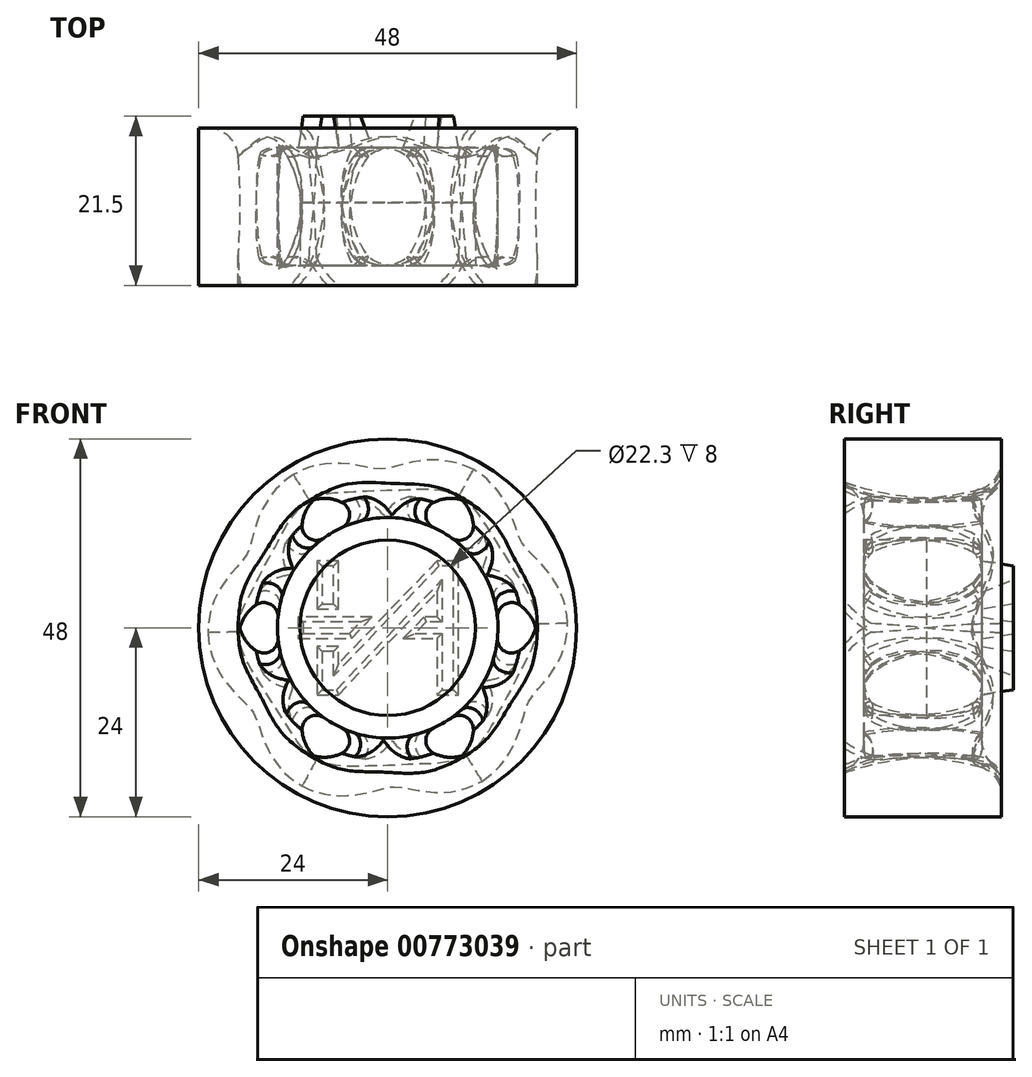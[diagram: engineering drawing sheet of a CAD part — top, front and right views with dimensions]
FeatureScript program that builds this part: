
annotation { "Feature Type Name" : "Feature", "Feature Type Description" : "" }
export const myFeature = defineFeature(function(context is Context, id is Id, definition is map)
    precondition{}
    {
        {
            var Q0;
            Q0=qCreatedBy(makeId("Front.planeOp"),FACE);
            var sketch = newSketch(context, id + "F0", { "sketchPlane" : qUnion([Q0])});
            skCircle(sketch, "E0", {"center": v(0, 0) * mm, "radius": 24 * mm});
            skCircle(sketch, "E1", {"center": v(0, 0) * mm, "radius": 19 * mm});
            skSolve(sketch);
        }
        {
            var Q0;
            Q0 = qSketchRegion(id + "F0", true);
            extrude(context, id + "F1", {"entities" : qUnion([Q0]), "endBound" : BoundingType.SYMMETRIC, "depth" : 20 * mm, "offsetDistance" : 25 * mm});
        }
        {
            var Q0;
            Q0=qCreatedBy(makeId("Front.planeOp"),FACE);
            var sketch = newSketch(context, id + "F2", { "sketchPlane" : qUnion([Q0])});
            skCircle(sketch, "E2", {"center": v(0, 0) * mm, "radius": 14 * mm});
            skSolve(sketch);
        }
        {
            var Q0;
            Q0 = qSketchRegion(id + "F2", true);
            extrude(context, id + "F3", {"entities" : qUnion([Q0]), "endBound" : BoundingType.SYMMETRIC, "depth" : 15 * mm, "offsetDistance" : 25 * mm});
        }
        {
            var Q0;
            Q0=qCreatedBy(makeId("Top.planeOp"),FACE);
            var sketch = newSketch(context, id + "F4", { "sketchPlane" : qUnion([Q0])});
            skEllipse(sketch, "E3", {"center": v(0, 0) * mm, "majorRadius": 7.5 * mm, "minorRadius": 3 * mm, "majorAxis": v(0.08, -1)});
            skSolve(sketch);
        }
        {
            var Q0;
            Q0 = qSketchRegion(id + "F4", true);
            extrude(context, id + "F5", {"entities" : qUnion([Q0]), "depth" : 22.2 * mm, "offsetDistance" : 25 * mm});
        }
        {
            var Q0;
            Q0=makeQuery(id+"F5.opExtrude","SWEPT_BODY",BODY,{"disambiguationData":[OSD([sQuery(id+"F4.wireOp",EDGE,"E3")])]});
            var Q1;
            Q1=makeQuery(id+"F3.opExtrude","CAP_EDGE",EDGE,{"disambiguationData":[OSD([sQuery(id+"F2.wireOp",EDGE,"E2")])],"isStart":true});
            circularPattern(context, id + "F6", {"entities" : qUnion([Q0]), "axis" : qUnion([Q1]), "angle" : 360 * degree, "instanceCount" : 6, "equalSpace" : true});
        }
        {
            var Q0;
            Q0=makeQuery(id+"F3.opExtrude","CAP_FACE",FACE,{"disambiguationData":[OSD([sQuery(id+"F2.wireOp",EDGE,"E2")])],"isStart":false});
            var sketch = newSketch(context, id + "F7", { "sketchPlane" : qUnion([Q0])});
            skPoint(sketch, "E4", {"position": v(0, -1.13) * mm});
            skSolve(sketch);
        }
        {
            var Q0;
            Q0=makeQuery(id+"F7.imprint","IMPRINT",FACE,{"disambiguationData":[TD([[makeQuery(id+"F7.imprint","IMPRINT",EDGE,{"derivedFrom":makeQuery(id+"F3.opExtrude","CAP_EDGE",EDGE,{"disambiguationData":[OSD([sQuery(id+"F2.wireOp",EDGE,"E2")])],"isStart":false})}),1.0]])]});
            var sketch = newSketch(context, id + "F8", { "sketchPlane" : qUnion([Q0])});
            skCircle(sketch, "E5", {"center": v(0, 0) * mm, "radius": 11.15 * mm});
            skSolve(sketch);
        }
        {
            var Q0;
            Q0 = qSketchRegion(id + "F8", true);
            extrude(context, id + "F9", {"entities" : qUnion([Q0]), "operationType" : NewBodyOperationType.REMOVE, "oppositeDirection" : true, "depth" : 8 * mm, "offsetDistance" : 25 * mm});
        }
        {
            var Q0;
            Q0=makeQuery(id+"F3.opExtrude","SWEPT_BODY",BODY,{"disambiguationData":[OSD([sQuery(id+"F2.wireOp",EDGE,"E2")])]});
            var Q1;
            Q1=makeQuery(id+"F1.opExtrude","SWEPT_BODY",BODY,{"disambiguationData":[OSD([sQuery(id+"F0.wireOp",EDGE,"E0"),sQuery(id+"F0.wireOp",EDGE,"E1")])]});
            var Q2;
            Q2=makeQuery(id+"F5.opExtrude","SWEPT_BODY",BODY,{"disambiguationData":[OSD([sQuery(id+"F4.wireOp",EDGE,"E3")])]});
            var Q3;
            Q3=makeQuery(id+"F6.opPattern","COPY",BODY,{"derivedFrom":makeQuery(id+"F5.opExtrude","SWEPT_BODY",BODY,{"disambiguationData":[OSD([sQuery(id+"F4.wireOp",EDGE,"E3")])]}),"instanceName":"2"});
            var Q4;
            Q4=makeQuery(id+"F6.opPattern","COPY",BODY,{"derivedFrom":makeQuery(id+"F5.opExtrude","SWEPT_BODY",BODY,{"disambiguationData":[OSD([sQuery(id+"F4.wireOp",EDGE,"E3")])]}),"instanceName":"4"});
            var Q5;
            Q5=makeQuery(id+"F6.opPattern","COPY",BODY,{"derivedFrom":makeQuery(id+"F5.opExtrude","SWEPT_BODY",BODY,{"disambiguationData":[OSD([sQuery(id+"F4.wireOp",EDGE,"E3")])]}),"instanceName":"5"});
            var Q6;
            Q6=makeQuery(id+"F6.opPattern","COPY",BODY,{"derivedFrom":makeQuery(id+"F5.opExtrude","SWEPT_BODY",BODY,{"disambiguationData":[OSD([sQuery(id+"F4.wireOp",EDGE,"E3")])]}),"instanceName":"1"});
            var Q7;
            Q7=makeQuery(id+"F6.opPattern","COPY",BODY,{"derivedFrom":makeQuery(id+"F5.opExtrude","SWEPT_BODY",BODY,{"disambiguationData":[OSD([sQuery(id+"F4.wireOp",EDGE,"E3")])]}),"instanceName":"3"});
            booleanBodies(context, id + "F10", {"operationType" : BooleanOperationType.UNION, "tools" : qUnion([Q0, Q1, Q2, Q3, Q4, Q5, Q6, Q7])});
        }
        {
            var Q0;
            Q0=makeQuery(id+"F10.opBoolean","INTERSECT",EDGE,{"derivedFrom":[makeQuery(id+"F1.opExtrude","SWEPT_FACE",FACE,{"disambiguationData":[OSD([sQuery(id+"F0.wireOp",EDGE,"E1")])]}),makeQuery(id+"F6.opPattern","COPY",FACE,{"derivedFrom":makeQuery(id+"F5.opExtrude","SWEPT_FACE",FACE,{"disambiguationData":[OSD([sQuery(id+"F4.wireOp",EDGE,"E3")])]}),"instanceName":"2"})]});
            var Q1;
            Q1=makeQuery(id+"F10.opBoolean","INTERSECT",EDGE,{"derivedFrom":[makeQuery(id+"F1.opExtrude","SWEPT_FACE",FACE,{"disambiguationData":[OSD([sQuery(id+"F0.wireOp",EDGE,"E1")])]}),makeQuery(id+"F6.opPattern","COPY",FACE,{"derivedFrom":makeQuery(id+"F5.opExtrude","SWEPT_FACE",FACE,{"disambiguationData":[OSD([sQuery(id+"F4.wireOp",EDGE,"E3")])]}),"instanceName":"3"})]});
            var Q2;
            Q2=makeQuery(id+"F10.opBoolean","INTERSECT",EDGE,{"derivedFrom":[makeQuery(id+"F1.opExtrude","SWEPT_FACE",FACE,{"disambiguationData":[OSD([sQuery(id+"F0.wireOp",EDGE,"E1")])]}),makeQuery(id+"F6.opPattern","COPY",FACE,{"derivedFrom":makeQuery(id+"F5.opExtrude","SWEPT_FACE",FACE,{"disambiguationData":[OSD([sQuery(id+"F4.wireOp",EDGE,"E3")])]}),"instanceName":"4"})]});
            var Q3;
            Q3=makeQuery(id+"F10.opBoolean","INTERSECT",EDGE,{"derivedFrom":[makeQuery(id+"F1.opExtrude","SWEPT_FACE",FACE,{"disambiguationData":[OSD([sQuery(id+"F0.wireOp",EDGE,"E1")])]}),makeQuery(id+"F6.opPattern","COPY",FACE,{"derivedFrom":makeQuery(id+"F5.opExtrude","SWEPT_FACE",FACE,{"disambiguationData":[OSD([sQuery(id+"F4.wireOp",EDGE,"E3")])]}),"instanceName":"5"})]});
            var Q4;
            Q4=makeQuery(id+"F10.opBoolean","INTERSECT",EDGE,{"derivedFrom":[makeQuery(id+"F1.opExtrude","SWEPT_FACE",FACE,{"disambiguationData":[OSD([sQuery(id+"F0.wireOp",EDGE,"E1")])]}),makeQuery(id+"F5.opExtrude","SWEPT_FACE",FACE,{"disambiguationData":[OSD([sQuery(id+"F4.wireOp",EDGE,"E3")])]})]});
            var Q5;
            Q5=makeQuery(id+"F10.opBoolean","INTERSECT",EDGE,{"derivedFrom":[makeQuery(id+"F1.opExtrude","SWEPT_FACE",FACE,{"disambiguationData":[OSD([sQuery(id+"F0.wireOp",EDGE,"E1")])]}),makeQuery(id+"F6.opPattern","COPY",FACE,{"derivedFrom":makeQuery(id+"F5.opExtrude","SWEPT_FACE",FACE,{"disambiguationData":[OSD([sQuery(id+"F4.wireOp",EDGE,"E3")])]}),"instanceName":"1"})]});
            fillet(context, id + "F11", {"entities" : qUnion([Q0, Q1, Q2, Q3, Q4, Q5]), "radius" : 5 * mm, "tangentPropagation" : true, "allowEdgeOverflow" : false});
        }
        {
            var Q0;
            Q0=makeQuery(id+"F11.opFillet","BLEND_EDGE",EDGE,{"disambiguationData":[OD(1.0)],"blendedFrom":[makeQuery(id+"F10.opBoolean","INTERSECT",EDGE,{"derivedFrom":[makeQuery(id+"F1.opExtrude","SWEPT_FACE",FACE,{"disambiguationData":[OSD([sQuery(id+"F0.wireOp",EDGE,"E1")])]}),makeQuery(id+"F6.opPattern","COPY",FACE,{"derivedFrom":makeQuery(id+"F5.opExtrude","SWEPT_FACE",FACE,{"disambiguationData":[OSD([sQuery(id+"F4.wireOp",EDGE,"E3")])]}),"instanceName":"2"})]}),makeQuery(id+"F3.opExtrude","SWEPT_FACE",FACE,{"disambiguationData":[OSD([sQuery(id+"F2.wireOp",EDGE,"E2")])]})],"blendedInto":[makeQuery(id+"F3.opExtrude","SWEPT_FACE",FACE,{"disambiguationData":[OSD([sQuery(id+"F2.wireOp",EDGE,"E2")])]})]});
            var Q1;
            Q1=makeQuery(id+"F11.opFillet","BLEND_EDGE",EDGE,{"disambiguationData":[OD(0.0)],"blendedFrom":[makeQuery(id+"F10.opBoolean","INTERSECT",EDGE,{"derivedFrom":[makeQuery(id+"F1.opExtrude","SWEPT_FACE",FACE,{"disambiguationData":[OSD([sQuery(id+"F0.wireOp",EDGE,"E1")])]}),makeQuery(id+"F6.opPattern","COPY",FACE,{"derivedFrom":makeQuery(id+"F5.opExtrude","SWEPT_FACE",FACE,{"disambiguationData":[OSD([sQuery(id+"F4.wireOp",EDGE,"E3")])]}),"instanceName":"3"})]}),makeQuery(id+"F3.opExtrude","SWEPT_FACE",FACE,{"disambiguationData":[OSD([sQuery(id+"F2.wireOp",EDGE,"E2")])]})],"blendedInto":[makeQuery(id+"F3.opExtrude","SWEPT_FACE",FACE,{"disambiguationData":[OSD([sQuery(id+"F2.wireOp",EDGE,"E2")])]})]});
            var Q2;
            Q2=makeQuery(id+"F11.opFillet","BLEND_EDGE",EDGE,{"disambiguationData":[OD(0.0)],"blendedFrom":[makeQuery(id+"F10.opBoolean","INTERSECT",EDGE,{"derivedFrom":[makeQuery(id+"F1.opExtrude","SWEPT_FACE",FACE,{"disambiguationData":[OSD([sQuery(id+"F0.wireOp",EDGE,"E1")])]}),makeQuery(id+"F6.opPattern","COPY",FACE,{"derivedFrom":makeQuery(id+"F5.opExtrude","SWEPT_FACE",FACE,{"disambiguationData":[OSD([sQuery(id+"F4.wireOp",EDGE,"E3")])]}),"instanceName":"4"})]}),makeQuery(id+"F3.opExtrude","SWEPT_FACE",FACE,{"disambiguationData":[OSD([sQuery(id+"F2.wireOp",EDGE,"E2")])]})],"blendedInto":[makeQuery(id+"F3.opExtrude","SWEPT_FACE",FACE,{"disambiguationData":[OSD([sQuery(id+"F2.wireOp",EDGE,"E2")])]})]});
            var Q3;
            Q3=makeQuery(id+"F11.opFillet","BLEND_EDGE",EDGE,{"disambiguationData":[OD(1.0)],"blendedFrom":[makeQuery(id+"F10.opBoolean","INTERSECT",EDGE,{"derivedFrom":[makeQuery(id+"F1.opExtrude","SWEPT_FACE",FACE,{"disambiguationData":[OSD([sQuery(id+"F0.wireOp",EDGE,"E1")])]}),makeQuery(id+"F6.opPattern","COPY",FACE,{"derivedFrom":makeQuery(id+"F5.opExtrude","SWEPT_FACE",FACE,{"disambiguationData":[OSD([sQuery(id+"F4.wireOp",EDGE,"E3")])]}),"instanceName":"5"})]}),makeQuery(id+"F3.opExtrude","SWEPT_FACE",FACE,{"disambiguationData":[OSD([sQuery(id+"F2.wireOp",EDGE,"E2")])]})],"blendedInto":[makeQuery(id+"F3.opExtrude","SWEPT_FACE",FACE,{"disambiguationData":[OSD([sQuery(id+"F2.wireOp",EDGE,"E2")])]})]});
            var Q4;
            Q4=makeQuery(id+"F11.opFillet","BLEND_EDGE",EDGE,{"disambiguationData":[OD(1.0)],"blendedFrom":[makeQuery(id+"F10.opBoolean","INTERSECT",EDGE,{"derivedFrom":[makeQuery(id+"F1.opExtrude","SWEPT_FACE",FACE,{"disambiguationData":[OSD([sQuery(id+"F0.wireOp",EDGE,"E1")])]}),makeQuery(id+"F5.opExtrude","SWEPT_FACE",FACE,{"disambiguationData":[OSD([sQuery(id+"F4.wireOp",EDGE,"E3")])]})]}),makeQuery(id+"F3.opExtrude","SWEPT_FACE",FACE,{"disambiguationData":[OSD([sQuery(id+"F2.wireOp",EDGE,"E2")])]})],"blendedInto":[makeQuery(id+"F3.opExtrude","SWEPT_FACE",FACE,{"disambiguationData":[OSD([sQuery(id+"F2.wireOp",EDGE,"E2")])]})]});
            var Q5;
            Q5=makeQuery(id+"F11.opFillet","BLEND_EDGE",EDGE,{"disambiguationData":[OD(1.0)],"blendedFrom":[makeQuery(id+"F10.opBoolean","INTERSECT",EDGE,{"derivedFrom":[makeQuery(id+"F1.opExtrude","SWEPT_FACE",FACE,{"disambiguationData":[OSD([sQuery(id+"F0.wireOp",EDGE,"E1")])]}),makeQuery(id+"F6.opPattern","COPY",FACE,{"derivedFrom":makeQuery(id+"F5.opExtrude","SWEPT_FACE",FACE,{"disambiguationData":[OSD([sQuery(id+"F4.wireOp",EDGE,"E3")])]}),"instanceName":"1"})]}),makeQuery(id+"F3.opExtrude","SWEPT_FACE",FACE,{"disambiguationData":[OSD([sQuery(id+"F2.wireOp",EDGE,"E2")])]})],"blendedInto":[makeQuery(id+"F3.opExtrude","SWEPT_FACE",FACE,{"disambiguationData":[OSD([sQuery(id+"F2.wireOp",EDGE,"E2")])]})]});
            fillet(context, id + "F12", {"entities" : qUnion([Q0, Q1, Q2, Q3, Q4, Q5]), "radius" : 1.79 * mm, "tangentPropagation" : true, "allowEdgeOverflow" : false});
        }
        {
            var Q0;
            Q0=makeQuery(id+"F3.opExtrude","CAP_FACE",FACE,{"disambiguationData":[OSD([sQuery(id+"F2.wireOp",EDGE,"E2")])],"isStart":true});
            var sketch = newSketch(context, id + "F13", { "sketchPlane" : qUnion([Q0])});
            skLineSegment(sketch, "E6", {"start": v(-14, 0) * mm, "end": v(14, 0) * mm, "construction": true});
            skLineSegment(sketch, "E7", {"start": v(0, -14) * mm, "end": v(0, 14) * mm, "construction": true});
            skLineSegment(sketch, "E8", {"start": v(-9, -8.5) * mm, "end": v(-9, 8.5) * mm});
            skLineSegment(sketch, "E9", {"start": v(9, -8.5) * mm, "end": v(9, -2.37) * mm});
            skLineSegment(sketch, "E10", {"start": v(-9, -8.5) * mm, "end": v(-6.26, -8.5) * mm});
            skLineSegment(sketch, "E11", {"start": v(-6.26, -8.5) * mm, "end": v(-6.26, -1.37) * mm});
            skLineSegment(sketch, "E12", {"start": v(-6.26, 8.5) * mm, "end": v(-9, 8.5) * mm});
            skLineSegment(sketch, "E13.MirrorCS", {"start": v(6.26, -4.54) * mm, "end": v(6.26, -2.37) * mm});
            skLineSegment(sketch, "E14.MirrorCS", {"start": v(9, -8.5) * mm, "end": v(6.26, -8.5) * mm});
            skLineSegment(sketch, "E15.MirrorCS", {"start": v(6.26, 8.5) * mm, "end": v(9, 8.5) * mm});
            skLineSegment(sketch, "E16", {"start": v(6.26, -4.54) * mm, "end": v(-6.26, 8.5) * mm});
            skLineSegment(sketch, "E17", {"start": v(6.26, -8.5) * mm, "end": v(-6.26, 4.54) * mm});
            skLineSegment(sketch, "E18", {"start": v(-6.26, 1.37) * mm, "end": v(-4.6, 1.37) * mm});
            skLineSegment(sketch, "E19", {"start": v(11.37, 1.37) * mm, "end": v(11.37, -1.37) * mm});
            skLineSegment(sketch, "E20", {"start": v(11.37, -1.37) * mm, "end": v(4.6, -1.37) * mm});
            skLineSegment(sketch, "E21", {"start": v(-1.97, -1.37) * mm, "end": v(-4.6, 1.37) * mm});
            skLineSegment(sketch, "E22", {"start": v(4.6, -1.37) * mm, "end": v(1.97, 1.37) * mm});
            skLineSegment(sketch, "E23", {"start": v(6.26, -2.37) * mm, "end": v(9, -2.37) * mm});
            skLineSegment(sketch, "E24", {"start": v(6.26, 2.37) * mm, "end": v(9, 2.37) * mm});
            skLineSegment(sketch, "E25.trimOffspring", {"start": v(-1.97, -1.37) * mm, "end": v(-6.26, -1.37) * mm});
            skLineSegment(sketch, "E26.trimOffspring", {"start": v(-3.21, 1.37) * mm, "end": v(0.58, 1.37) * mm});
            skLineSegment(sketch, "E27.trimOffspring", {"start": v(1.97, 1.37) * mm, "end": v(11.37, 1.37) * mm});
            skLineSegment(sketch, "E28.trimOffspring", {"start": v(-6.26, 1.37) * mm, "end": v(-6.26, 4.54) * mm});
            skPoint(sketch, "E29.orphan", {"position": v(11.37, -2.37) * mm});
            skLineSegment(sketch, "E30.trimOffspring", {"start": v(9, 2.37) * mm, "end": v(9, 8.5) * mm});
            skLineSegment(sketch, "E31.trimOffspring", {"start": v(6.26, 2.37) * mm, "end": v(6.26, 8.5) * mm});
            skSolve(sketch);
        }
        {
            var Q0;
            Q0=makeQuery(id+"F13.imprint","IMPRINT",FACE,{"disambiguationData":[TD([[makeQuery(id+"F13.imprint","IMPRINT",EDGE,{"derivedFrom":sQuery(id+"F13.wireOp",EDGE,"E8")}),-1.0]])]});
            var Q1;
            Q1=makeQuery(id+"F13.imprint","IMPRINT",FACE,{"disambiguationData":[TD([[makeQuery(id+"F13.imprint","IMPRINT",EDGE,{"derivedFrom":sQuery(id+"F13.wireOp",EDGE,"E9")}),1.0]])]});
            var Q2;
            Q2=makeQuery(id+"F13.imprint","IMPRINT",FACE,{"disambiguationData":[TD([[makeQuery(id+"F13.imprint","IMPRINT",EDGE,{"derivedFrom":sQuery(id+"F13.wireOp",EDGE,"E19")}),-1.0]])]});
            var Q3;
            Q3=makeQuery(id+"F13.imprint","IMPRINT",FACE,{"disambiguationData":[TD([[makeQuery(id+"F13.imprint","IMPRINT",EDGE,{"derivedFrom":sQuery(id+"F13.wireOp",EDGE,"E15.MirrorCS")}),-1.0]])]});
            extrude(context, id + "F14", {"entities" : qUnion([Q0, Q1, Q2, Q3]), "operationType" : NewBodyOperationType.ADD, "depth" : 4 * mm, "offsetDistance" : 25 * mm, "hasDraft" : true, "draftAngle" : 9 * degree, "draftPullDirection" : true});
        }
        {
            var Q0;
            Q0=makeQuery(id+"F1.opExtrude","CAP_EDGE",EDGE,{"disambiguationData":[OSD([sQuery(id+"F0.wireOp",EDGE,"E1")])],"isStart":true});
            var Q1;
            Q1=makeQuery(id+"F1.opExtrude","CAP_EDGE",EDGE,{"disambiguationData":[OSD([sQuery(id+"F0.wireOp",EDGE,"E1")])],"isStart":true});
            var Q2;
            Q2=makeQuery(id+"F1.opExtrude","CAP_EDGE",EDGE,{"disambiguationData":[OSD([sQuery(id+"F0.wireOp",EDGE,"E1")])],"isStart":true});
            var Q3;
            Q3=makeQuery(id+"F1.opExtrude","CAP_EDGE",EDGE,{"disambiguationData":[OSD([sQuery(id+"F0.wireOp",EDGE,"E1")])],"isStart":true});
            var Q4;
            Q4=makeQuery(id+"F1.opExtrude","CAP_EDGE",EDGE,{"disambiguationData":[OSD([sQuery(id+"F0.wireOp",EDGE,"E1")])],"isStart":true});
            var Q5;
            Q5=makeQuery(id+"F1.opExtrude","CAP_EDGE",EDGE,{"disambiguationData":[OSD([sQuery(id+"F0.wireOp",EDGE,"E1")])],"isStart":true});
            fillet(context, id + "F15", {"entities" : qUnion([Q0, Q1, Q2, Q3, Q4, Q5]), "radius" : 3.86 * mm, "tangentPropagation" : true, "allowEdgeOverflow" : false});
        }
    });
